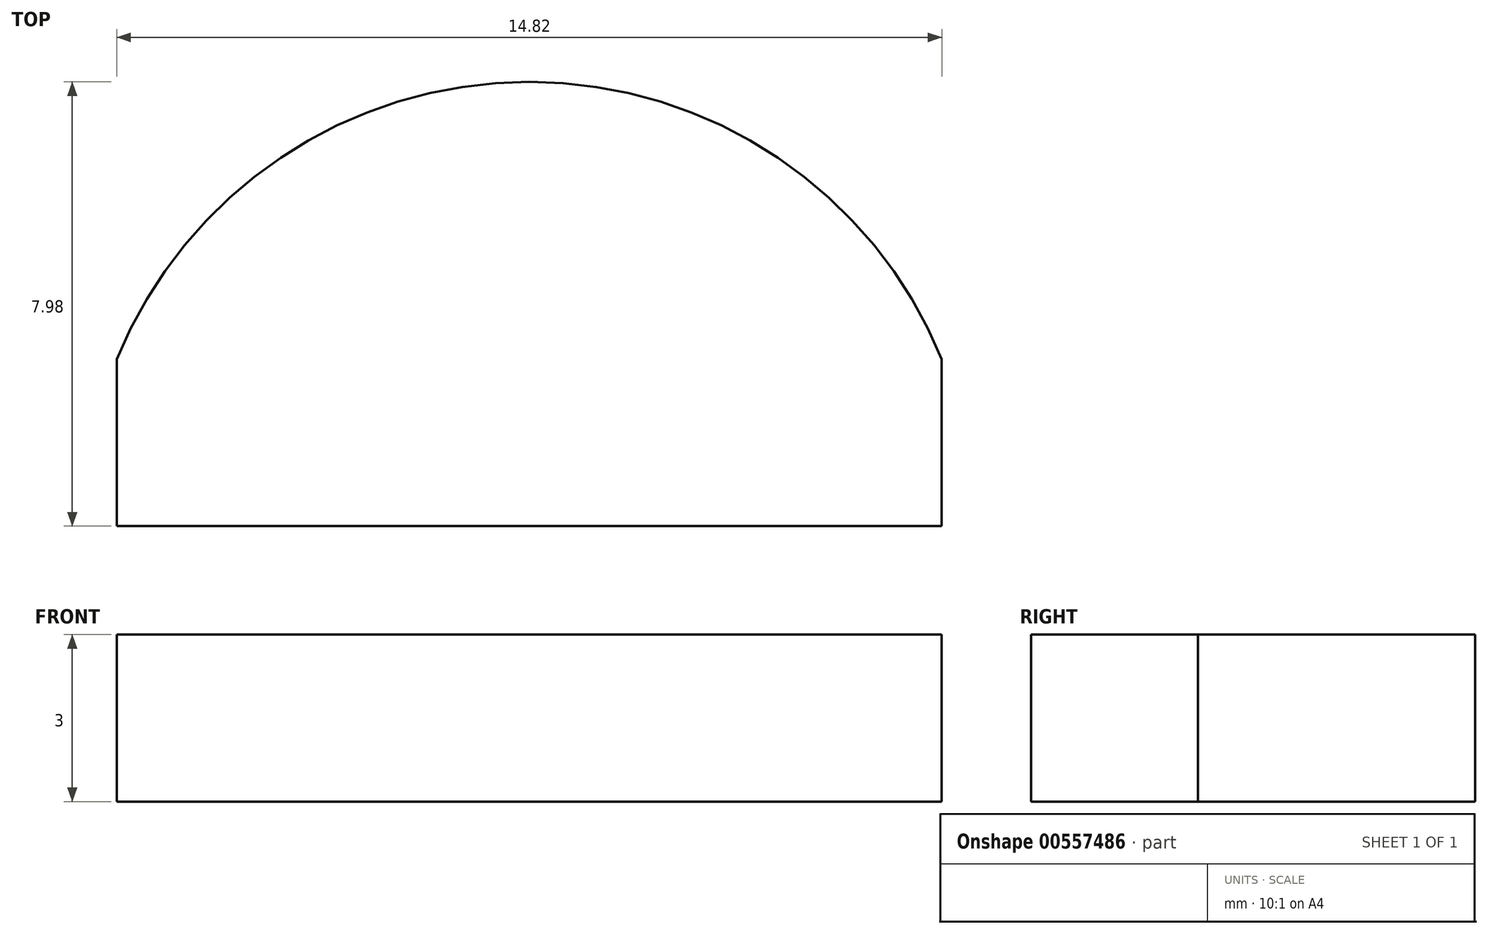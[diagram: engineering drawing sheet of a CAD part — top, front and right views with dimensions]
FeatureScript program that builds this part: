
annotation { "Feature Type Name" : "Feature", "Feature Type Description" : "" }
export const myFeature = defineFeature(function(context is Context, id is Id, definition is map)
    precondition{}
    {
        {
            var Q0;
            Q0=qCreatedBy(makeId("Top.planeOp"),FACE);
            var sketch = newSketch(context, id + "F0", { "sketchPlane" : qUnion([Q0])});
            skArc(sketch, "E0", {"start": v(7.4, 3) * mm, "mid": v(0, 7.98) * mm, "end": v(-7.4, 3) * mm});
            skLineSegment(sketch, "E1", {"start": v(-7.42, 3) * mm, "end": v(-7.4, 3) * mm});
            skLineSegment(sketch, "E2", {"start": v(-7.4, 3) * mm, "end": v(-7.4, 0) * mm});
            skPoint(sketch, "E3.orphan", {"position": v(-8, 0) * mm});
            skLineSegment(sketch, "E4", {"start": v(7.4, 0) * mm, "end": v(7.4, 3) * mm});
            skPoint(sketch, "E5.start.orphan", {"position": v(8, 0) * mm});
            skLineSegment(sketch, "E6", {"start": v(-7.4, 0) * mm, "end": v(7.4, 0) * mm});
            skSolve(sketch);
        }
        {
            var Q0;
            Q0 = qSketchRegion(id + "F0", true);
            extrude(context, id + "F1", {"entities" : qUnion([Q0]), "depth" : 3 * mm, "offsetDistance" : 25 * mm});
        }
    });
